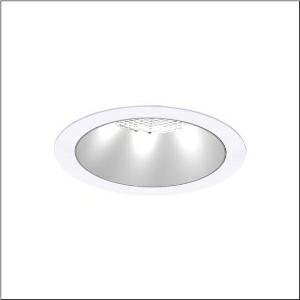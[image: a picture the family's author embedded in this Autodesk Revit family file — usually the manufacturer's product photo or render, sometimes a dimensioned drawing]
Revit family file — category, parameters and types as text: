
# Revit family: lunis_21_xl_51db19ef91c
name_source: partatom
category: Lighting Fixtures
units: mm (PartAtom-declared; Revit-internal decimal feet)

## family parameters
Cut with Voids When Loaded = No
Host = Face
Light Source = No
Part Type = Normal
Room Calculation Point = No
Round Connector Dimension = Use Diameter
Shared = No

## types (1)
- --- (1 x LED, 3900 lm, 25.4 W, 6500K)
    Apparent Load = 25 VA
    CIE Flux Codes = 91 99 100 100 100
    Color Rendering = 80
    Color Temperature = 6500K
    Default Elevation = 1800 mm
    Description = Lunis 21,  XL, downlight, light control with lens, of PMMA, anti glare with reflector, of PC, matt, light emission: direct distribution, LED rated luminous flux: 2.310lm, light colour: 830/840/865, with terminal, 5-pole, mains connection: 220..240V, AC/DC, 0/50..60Hz, housing, round, of diecast aluminium, traffic white (RAL 9016), diameter: 230mm, clamping range: 1..40mm, protection rating (complete): IP20, protection rating (on room side): IP54, insulation class (complete): insulation class II (safety insulation), certification: CE, impact resistance: IK03, packaging unit: 1 piece
    Height = 0 mm  [stored 0 ft]
    Lamp = 1 x LED
    Lamp Light Flux = 3900 lm
    Lamp Power = 25.4 W
    Lamp count = 1
    Length = 230 mm
    Luminous efficacy = 154 lm/W
    Manufacturer = Siteco
    ModVariant = No
    Model = 51DB19EF91C
    Mounting Place = Ceiling
    Mounting Type = Recessed
    Number of Poles = 1
    OnlyDefault = Yes
    Power Factor = 1
    Product Name = Lunis 21 XL
    Product group = downlight
    ProductGroupID = 400
    Protection Class = Protection class II
    Protection Degree = IP 20
    RLX_Detail_Level = 1
    RLX_Emergency_Light_Flux = 0 lm
    RLX_Emergency_Type = 0
    RLX_Emergency_Type_DB = No
    RlxData = <blob elided: 23037 chars, md5=a5b3671c>
    Socket = socket
    Standby Power = 0 W
    System Light Flux = 3900 lm
    System Power = 25 W
    Type Comments = individual setting: colour temperature 6500K, luminous flux: 100 % | (ON | ON | OFF | OFF) | 700 mA
    Type Image = l_1291163.jpg
    URL = http://relux.com
    VarID = @adj_018718
    Voltage = 0 V
    Weight = 0.00 kg
    Width = 0 mm  [stored 0 ft]

note: [stored X ft] marks values corroborated as IEEE doubles in the binary element streams (Revit-internal decimal feet)

## geometry (parser evidence)
native form markers: Blend x4, Sweep x9
no freeform markers — native parametric forms only
